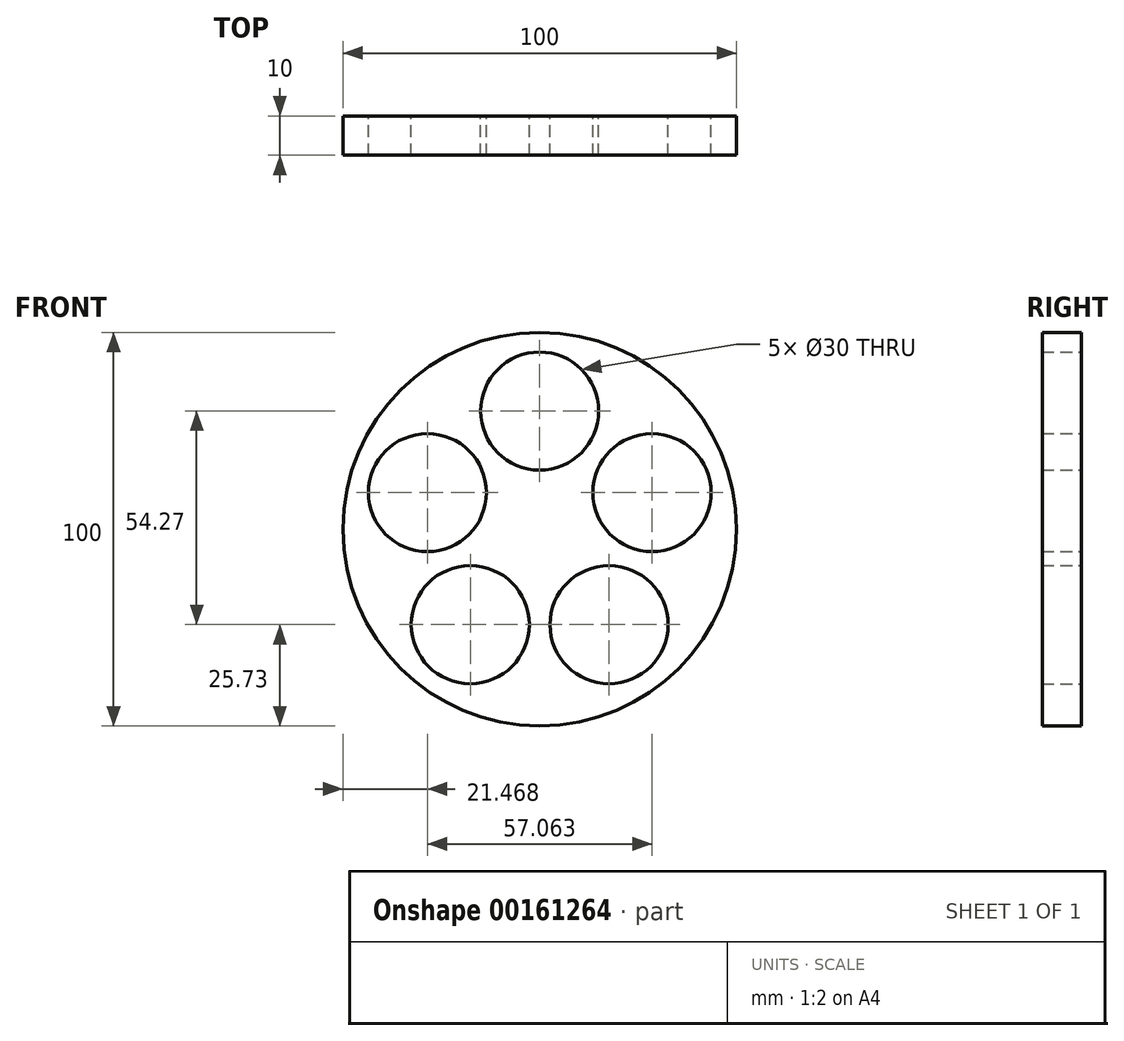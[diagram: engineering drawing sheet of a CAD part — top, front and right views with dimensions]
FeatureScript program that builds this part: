
annotation { "Feature Type Name" : "Feature", "Feature Type Description" : "" }
export const myFeature = defineFeature(function(context is Context, id is Id, definition is map)
    precondition{}
    {
        {
            var Q0;
            Q0=qCreatedBy(makeId("Front.planeOp"),FACE);
            var sketch = newSketch(context, id + "F0", { "sketchPlane" : qUnion([Q0])});
            skCircle(sketch, "E0", {"center": v(0, 0) * mm, "radius": 50 * mm});
            skCircle(sketch, "E1", {"center": v(0, 30) * mm, "radius": 15 * mm});
            skCircle(sketch, "E2.0", {"center": v(0, 30) * mm, "radius": 10 * mm});
            skCircle(sketch, "E3.1.0", {"center": v(-28.53, 9.27) * mm, "radius": 10 * mm});
            skCircle(sketch, "E3.1.1", {"center": v(-28.53, 9.27) * mm, "radius": 15 * mm});
            skCircle(sketch, "E3.2.0", {"center": v(-17.63, -24.27) * mm, "radius": 10 * mm});
            skCircle(sketch, "E3.2.1", {"center": v(-17.63, -24.27) * mm, "radius": 15 * mm});
            skCircle(sketch, "E3.3.0", {"center": v(17.63, -24.27) * mm, "radius": 10 * mm});
            skCircle(sketch, "E3.3.1", {"center": v(17.63, -24.27) * mm, "radius": 15 * mm});
            skCircle(sketch, "E3.4.0", {"center": v(28.53, 9.27) * mm, "radius": 10 * mm});
            skCircle(sketch, "E3.4.1", {"center": v(28.53, 9.27) * mm, "radius": 15 * mm});
            skSolve(sketch);
        }
        {
            var Q0;
            Q0 = qSketchRegion(id + "F0", true);
            extrude(context, id + "F1", {"entities" : qUnion([Q0]), "depth" : 10 * mm, "symmetric" : true});
        }
    });
